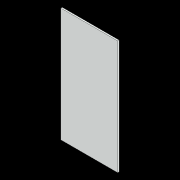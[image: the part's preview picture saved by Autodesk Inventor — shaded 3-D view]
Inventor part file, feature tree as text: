
AUTODESK INVENTOR PART (.ipt)
format: ipt  version: 2022 (Build 260153000, 153)  size: 77,312 bytes
history: native  units: in
note: dims shown in document units (in); Inventor stores cm internally (conversion verified against a paired STEP export)
features: extrude x1, sketch x1
ambient origin geometry x8: Origin, YZ Plane, XZ Plane, XY Plane, X Axis, Y Axis, Z Axis, Center Point
bodies: Solid1 (feature_tree)
feature tree (2):
  extrude  "Extrusion1"  Depth=9.5079in
  sketch  "Sketch1"  dims[d0=4.7244in d1=9.5079in d2=0.1181in d3=0.0in]
